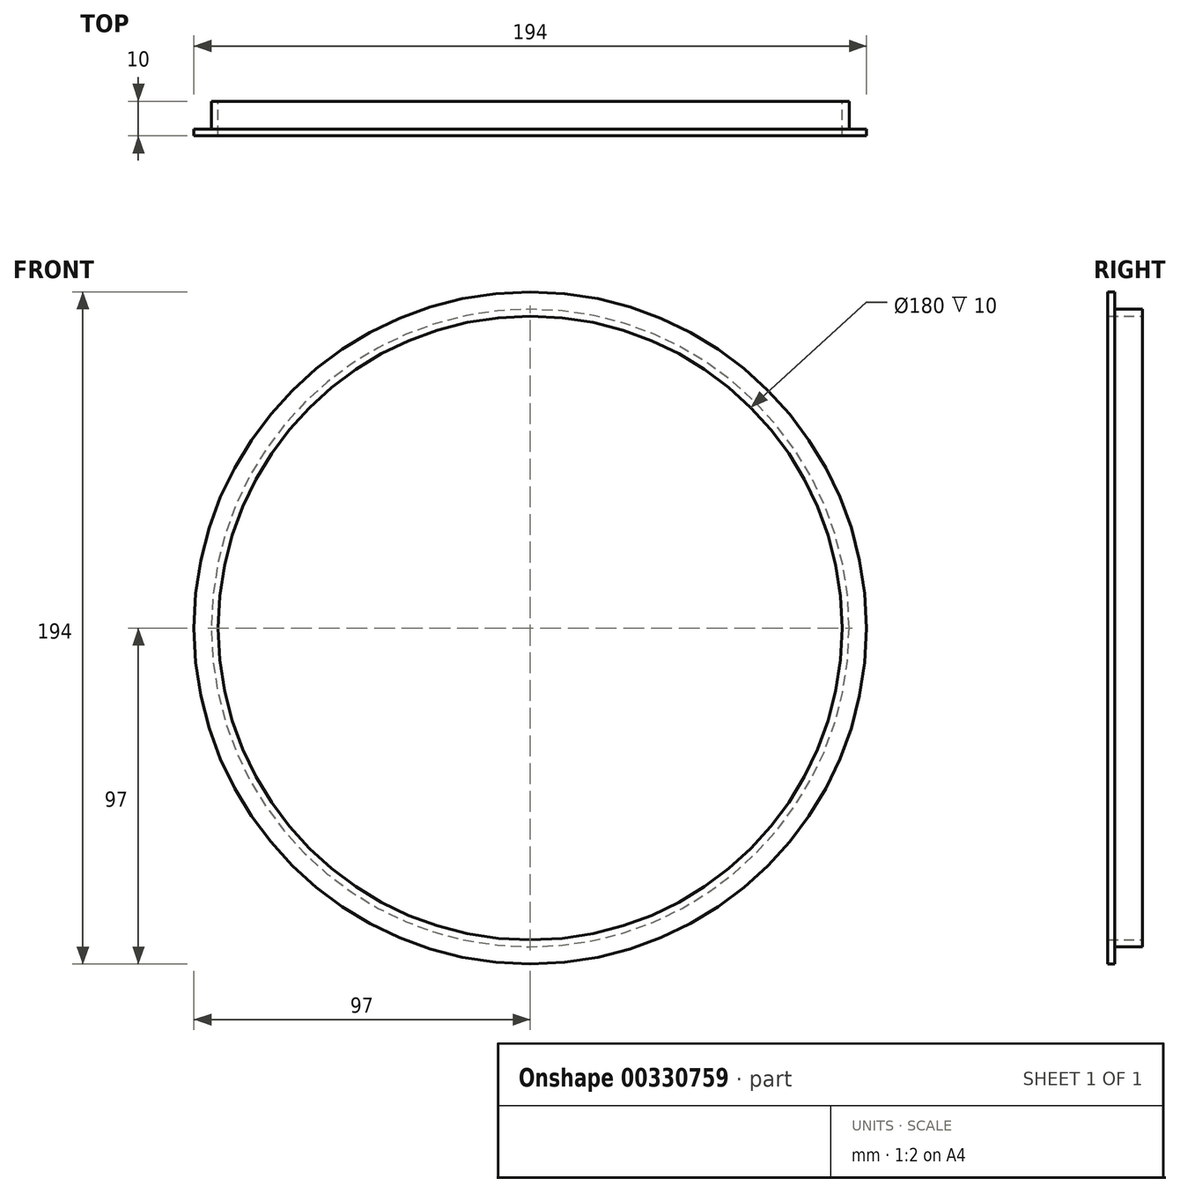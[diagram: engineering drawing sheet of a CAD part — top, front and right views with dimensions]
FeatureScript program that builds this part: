
annotation { "Feature Type Name" : "Feature", "Feature Type Description" : "" }
export const myFeature = defineFeature(function(context is Context, id is Id, definition is map)
    precondition{}
    {
        {
            var Q0;
            Q0=qCreatedBy(makeId("Front.planeOp"),FACE);
            var sketch = newSketch(context, id + "F0", { "sketchPlane" : qUnion([Q0])});
            skCircle(sketch, "E0", {"center": v(0, 0) * mm, "radius": 90 * mm});
            skCircle(sketch, "E1", {"center": v(0, 0) * mm, "radius": 97 * mm});
            skSolve(sketch);
        }
        {
            var Q0;
            Q0=makeQuery(id+"F0.imprint","IMPRINT",FACE,{"disambiguationData":[TD([[makeQuery(id+"F0.imprint","IMPRINT",EDGE,{"derivedFrom":sQuery(id+"F0.wireOp",EDGE,"E0")}),-1.0]])]});
            extrude(context, id + "F1", {"entities" : qUnion([Q0]), "depth" : 10 * mm});
        }
        {
            var Q0;
            Q0=makeQuery(id+"F1.opExtrude","CAP_FACE",FACE,{"disambiguationData":[OSD([sQuery(id+"F0.wireOp",EDGE,"E0"),sQuery(id+"F0.wireOp",EDGE,"E1")])],"isStart":true});
            var sketch = newSketch(context, id + "F2", { "sketchPlane" : qUnion([Q0])});
            skCircle(sketch, "E2", {"center": v(0, 0) * mm, "radius": 97 * mm});
            skCircle(sketch, "E3", {"center": v(0, 0) * mm, "radius": 92 * mm});
            skSolve(sketch);
        }
        {
            var Q0;
            Q0=makeQuery(id+"F2.imprint","IMPRINT",FACE,{"disambiguationData":[TD([[makeQuery(id+"F2.imprint","IMPRINT",EDGE,{"derivedFrom":sQuery(id+"F2.wireOp",EDGE,"E2")}),-1.0]])]});
            extrude(context, id + "F3", {"entities" : qUnion([Q0]), "operationType" : NewBodyOperationType.REMOVE, "oppositeDirection" : true, "depth" : 8 * mm});
        }
    });
